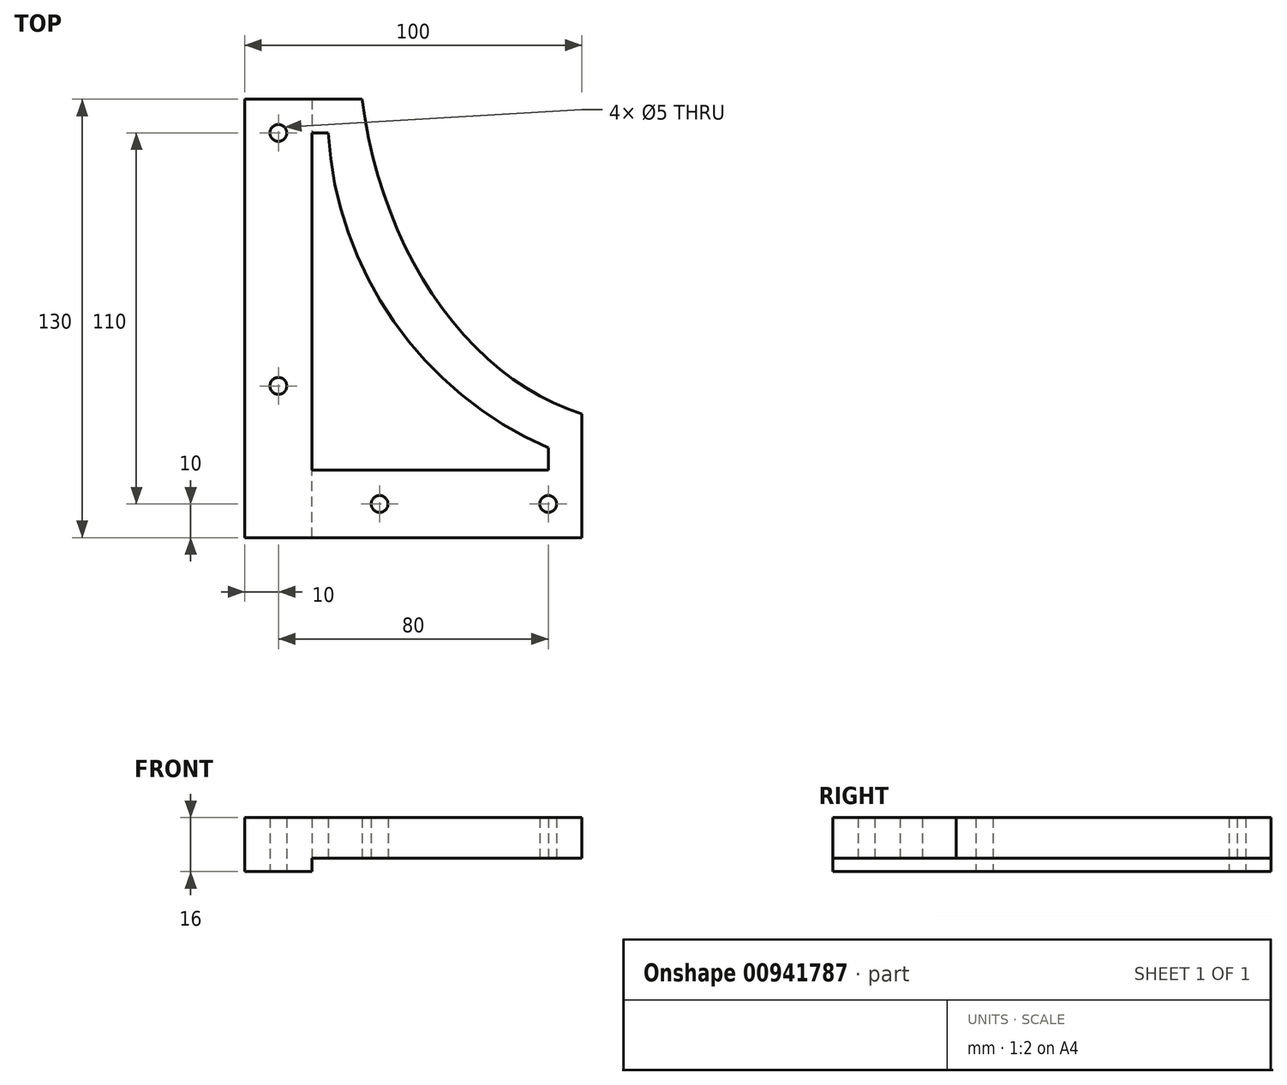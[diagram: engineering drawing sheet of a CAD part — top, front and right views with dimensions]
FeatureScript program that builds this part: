
annotation { "Feature Type Name" : "Feature", "Feature Type Description" : "" }
export const myFeature = defineFeature(function(context is Context, id is Id, definition is map)
    precondition{}
    {
        {
            var Q0;
            Q0=qCreatedBy(makeId("Top.planeOp"),FACE);
            var sketch = newSketch(context, id + "F0", { "sketchPlane" : qUnion([Q0])});
            skEllipticalArc(sketch, "E0", {});
            skLineSegment(sketch, "E1", {"start": v(-86.5, 0) * mm, "end": v(-86.5, -116.5) * mm});
            skPoint(sketch, "E1.endSnap0", {"position": v(0, -116.5) * mm});
            skLineSegment(sketch, "E2", {"start": v(-86.5, -116.5) * mm, "end": v(0, -116.5) * mm});
            skLineSegment(sketch, "E3", {"start": v(-86.5, 0) * mm, "end": v(-100, 0) * mm});
            skLineSegment(sketch, "E4", {"start": v(-100, 0) * mm, "end": v(-100, -130) * mm});
            skLineSegment(sketch, "E5", {"start": v(-100, -130) * mm, "end": v(0, -130) * mm});
            skLineSegment(sketch, "E6", {"start": v(0, -130) * mm, "end": v(0, -116.5) * mm});
            const initialGuessF0  = {"E0": [0, 0, 1, 0, 0.0865, 0.1165, 3.141592653589793, 4.71238898038469]};
            skSetInitialGuess(sketch, initialGuessF0);
            skSolve(sketch);
        }
        {
            var Q0;
            Q0=qSketchRegion(id+"F0",true);
            extrude(context, id + "F1", {"entities" : qUnion([Q0]), "depth" : 12 * mm, "offsetDistance" : 25 * mm});
        }
        {
            var Q0;
            Q0=makeQuery(id+"F1.opExtrude","SWEPT_FACE",FACE,{"disambiguationData":[OSD([sQuery(id+"F0.wireOp",EDGE,"E5")])]});
            var sketch = newSketch(context, id + "F2", { "sketchPlane" : qUnion([Q0])});
            skLineSegment(sketch, "E7.bottom", {"start": v(-100, 16) * mm, "end": v(0, 16) * mm});
            skLineSegment(sketch, "E7.top", {"start": v(-100, -4) * mm, "end": v(0, -4) * mm});
            skLineSegment(sketch, "E7.left", {"start": v(-100, 16) * mm, "end": v(-100, -4) * mm});
            skLineSegment(sketch, "E7.right", {"start": v(0, 16) * mm, "end": v(0, -4) * mm});
            skSolve(sketch);
        }
        {
            var Q0;
            Q0=qSketchRegion(id+"F2",true);
            extrude(context, id + "F3", {"entities" : qUnion([Q0]), "operationType" : NewBodyOperationType.ADD, "depth" : 5 * mm, "offsetDistance" : 25 * mm});
        }
        {
            var Q0;
            Q0=makeQuery(id+"F3.boolean.opBoolean","MERGE",FACE,{"derivedFrom":[makeQuery(id+"F1.opExtrude","SWEPT_FACE",FACE,{"disambiguationData":[OSD([sQuery(id+"F0.wireOp",EDGE,"E4")])]}),makeQuery(id+"F3.opExtrude","SWEPT_FACE",FACE,{"disambiguationData":[OSD([sQuery(id+"F2.wireOp",EDGE,"E7.left")])]})]});
            var sketch = newSketch(context, id + "F4", { "sketchPlane" : qUnion([Q0])});
            skLineSegment(sketch, "E8.bottom", {"start": v(135, 16) * mm, "end": v(0, 16) * mm});
            skLineSegment(sketch, "E8.top", {"start": v(135, -4) * mm, "end": v(0, -4) * mm});
            skLineSegment(sketch, "E8.left", {"start": v(135, 16) * mm, "end": v(135, -4) * mm});
            skLineSegment(sketch, "E8.right", {"start": v(0, 16) * mm, "end": v(0, -4) * mm});
            skSolve(sketch);
        }
        {
            var Q0;
            Q0=qSketchRegion(id+"F4",true);
            extrude(context, id + "F5", {"entities" : qUnion([Q0]), "operationType" : NewBodyOperationType.ADD, "depth" : 5 * mm, "offsetDistance" : 25 * mm});
        }
        {
            var Q0;
            Q0=makeQuery(id+"F5.boolean.opBoolean","MERGE",FACE,{"derivedFrom":[makeQuery(id+"F3.opExtrude","SWEPT_FACE",FACE,{"disambiguationData":[OSD([sQuery(id+"F2.wireOp",EDGE,"E7.bottom")])]}),makeQuery(id+"F5.opExtrude","SWEPT_FACE",FACE,{"disambiguationData":[OSD([sQuery(id+"F4.wireOp",EDGE,"E8.bottom")])]})]});
            var sketch = newSketch(context, id + "F6", { "sketchPlane" : qUnion([Q0])});
            skLineSegment(sketch, "E9", {"start": v(-105, 0) * mm, "end": v(-90, 0) * mm});
            skLineSegment(sketch, "E10", {"start": v(-90, 0) * mm, "end": v(-90, -120) * mm});
            skLineSegment(sketch, "E11", {"start": v(-90, -120) * mm, "end": v(0, -120) * mm});
            skLineSegment(sketch, "E12", {"start": v(0, -120) * mm, "end": v(0, -135) * mm});
            skLineSegment(sketch, "E13", {"start": v(0, -135) * mm, "end": v(-105, -135) * mm});
            skLineSegment(sketch, "E14", {"start": v(-105, -135) * mm, "end": v(-105, 0) * mm});
            skSolve(sketch);
        }
        {
            var Q0;
            Q0=makeQuery(id+"F5.boolean.opBoolean","MERGE",FACE,{"derivedFrom":[makeQuery(id+"F3.opExtrude","SWEPT_FACE",FACE,{"disambiguationData":[OSD([sQuery(id+"F2.wireOp",EDGE,"E7.top")])]}),makeQuery(id+"F5.opExtrude","SWEPT_FACE",FACE,{"disambiguationData":[OSD([sQuery(id+"F4.wireOp",EDGE,"E8.top")])]})]});
            var sketch = newSketch(context, id + "F7", { "sketchPlane" : qUnion([Q0])});
            skLineSegment(sketch, "E15", {"start": v(0, 150) * mm, "end": v(-120, 150) * mm});
            skLineSegment(sketch, "E16", {"start": v(-120, 150) * mm, "end": v(-120, 0) * mm});
            skLineSegment(sketch, "E17", {"start": v(-120, 0) * mm, "end": v(-105, 0) * mm});
            skLineSegment(sketch, "E18", {"start": v(-105, 0) * mm, "end": v(-105, 135) * mm});
            skLineSegment(sketch, "E19", {"start": v(-105, 135) * mm, "end": v(0, 135) * mm});
            skLineSegment(sketch, "E20", {"start": v(0, 135) * mm, "end": v(0, 150) * mm});
            skCircle(sketch, "E21", {"center": v(-110, 30) * mm, "radius": 2.5 * mm});
            skCircle(sketch, "E22", {"center": v(-110, 105) * mm, "radius": 2.5 * mm});
            skCircle(sketch, "E23", {"center": v(-80, 140) * mm, "radius": 2.5 * mm});
            skCircle(sketch, "E24", {"center": v(-30, 140) * mm, "radius": 2.5 * mm});
            skSolve(sketch);
        }
        {
            var Q0;
            Q0=qSketchRegion(id+"F7",true);
            extrude(context, id + "F8", {"entities" : qUnion([Q0]), "operationType" : NewBodyOperationType.ADD, "oppositeDirection" : true, "depth" : 25 * mm, "offsetDistance" : 25 * mm});
        }
        {
            var Q0;
            Q0=qSketchRegion(id+"F6",true);
            extrude(context, id + "F9", {"entities" : qUnion([Q0]), "operationType" : NewBodyOperationType.ADD, "depth" : 5 * mm, "offsetDistance" : 25 * mm});
        }
        {
            var Q0;
            Q0=qCreatedBy(makeId("Top.planeOp"),FACE);
            var sketch = newSketch(context, id + "F10", { "sketchPlane" : qUnion([Q0])});
            skLineSegment(sketch, "E25.bottom", {"start": v(0, 0) * mm, "end": v(-120, 0) * mm});
            skLineSegment(sketch, "E25.top", {"start": v(0, -20) * mm, "end": v(-120, -20) * mm});
            skLineSegment(sketch, "E25.left", {"start": v(0, 0) * mm, "end": v(0, -20) * mm});
            skLineSegment(sketch, "E25.right", {"start": v(-120, 0) * mm, "end": v(-120, -20) * mm});
            skLineSegment(sketch, "E26.bottom", {"start": v(0, 0) * mm, "end": v(-20, 0) * mm});
            skLineSegment(sketch, "E26.top", {"start": v(0, -150) * mm, "end": v(-20, -150) * mm});
            skLineSegment(sketch, "E26.left", {"start": v(0, 0) * mm, "end": v(0, -150) * mm});
            skLineSegment(sketch, "E26.right", {"start": v(-20, 0) * mm, "end": v(-20, -150) * mm});
            skSolve(sketch);
        }
        {
            var Q0;
            Q0=qSketchRegion(id+"F10",true);
            extrude(context, id + "F11", {"entities" : qUnion([Q0]), "operationType" : NewBodyOperationType.REMOVE, "endBound" : BoundingType.SYMMETRIC, "oppositeDirection" : true, "depth" : 50 * mm, "offsetDistance" : 25 * mm});
        }
        {
            var Q0;
            Q0=makeQuery(id+"F11.boolean.opBoolean","COPY",FACE,{"derivedFrom":makeQuery(id+"F11.opExtrude","SWEPT_FACE",FACE,{"disambiguationData":[OSD([sQuery(id+"F10.wireOp",EDGE,"E26.right")])]})});
            var sketch = newSketch(context, id + "F12", { "sketchPlane" : qUnion([Q0])});
            skLineSegment(sketch, "E27.bottom", {"start": v(-150, 21) * mm, "end": v(-20, 21) * mm});
            skLineSegment(sketch, "E27.top", {"start": v(-150, 12) * mm, "end": v(-20, 12) * mm});
            skLineSegment(sketch, "E27.left", {"start": v(-150, 21) * mm, "end": v(-150, 12) * mm});
            skLineSegment(sketch, "E27.right", {"start": v(-20, 21) * mm, "end": v(-20, 12) * mm});
            skSolve(sketch);
        }
        {
            var Q0;
            Q0=qSketchRegion(id+"F12",true);
            extrude(context, id + "F13", {"entities" : qUnion([Q0]), "operationType" : NewBodyOperationType.REMOVE, "endBound" : BoundingType.THROUGH_ALL, "oppositeDirection" : true, "depth" : 25 * mm, "offsetDistance" : 25 * mm});
        }
        {
            var Q0;
            Q0=makeQuery(id+"F1.opExtrude","CAP_FACE",FACE,{"disambiguationData":[OSD([sQuery(id+"F0.wireOp",EDGE,"E0"),sQuery(id+"F0.wireOp",EDGE,"E3"),sQuery(id+"F0.wireOp",EDGE,"E4"),sQuery(id+"F0.wireOp",EDGE,"E5"),sQuery(id+"F0.wireOp",EDGE,"E6")])],"isStart":true});
            var sketch = newSketch(context, id + "F14", { "sketchPlane" : qUnion([Q0])});
            skPoint(sketch, "E28.startSnap0", {"position": v(-20, 121.67) * mm});
            skLineSegment(sketch, "E29", {"start": v(-100, 130) * mm, "end": v(-100, 30) * mm});
            skLineSegment(sketch, "E30", {"start": v(-100, 30) * mm, "end": v(-95.22, 30) * mm});
            skLineSegment(sketch, "E31", {"start": v(-100, 130) * mm, "end": v(-30, 130) * mm});
            skLineSegment(sketch, "E32", {"start": v(-30, 130) * mm, "end": v(-30, 123.34) * mm});
            skArc(sketch, "E33", {"start": v(-30, 123.34) * mm, "mid": v(-75.82, 85.9) * mm, "end": v(-95.22, 30) * mm});
            skSolve(sketch);
        }
        {
            var Q0;
            Q0=qSketchRegion(id+"F14",true);
            extrude(context, id + "F15", {"entities" : qUnion([Q0]), "operationType" : NewBodyOperationType.REMOVE, "endBound" : BoundingType.THROUGH_ALL, "oppositeDirection" : true, "depth" : 25 * mm, "offsetDistance" : 25 * mm});
        }
        {
            var Q0;
            {var subQ1=sQuery(id+"F2.wireOp",EDGE,"E7.top");var subQ3=sQuery(id+"F2.wireOp",EDGE,"E7.right");var subQ4=sQuery(id+"F2.wireOp",EDGE,"E7.left");Q0=makeQuery(id+"F15.boolean.opBoolean","MERGE",FACE,{"derivedFrom":[makeQuery(id+"F3.boolean.opBoolean","SPLIT",FACE,{"disambiguationData":[TD([makeQuery(id+"F3.opExtrude","SWEPT_FACE",FACE,{"disambiguationData":[OSD([subQ1])]})])],"derivedFrom":makeQuery(id+"F3.opExtrude","CAP_FACE",FACE,{"disambiguationData":[OSD([sQuery(id+"F2.wireOp",EDGE,"E7.bottom"),subQ1,subQ4,subQ3])],"isStart":true})})],"fromTools":[makeQuery(id+"F15.opExtrude","SWEPT_FACE",FACE,{"disambiguationData":[OSD([sQuery(id+"F14.wireOp",EDGE,"E31")])]})]});}
            var sketch = newSketch(context, id + "F16", { "sketchPlane" : qUnion([Q0])});
            skLineSegment(sketch, "E34.bottom", {"start": v(20, -4) * mm, "end": v(20, -4) * mm});
            skLineSegment(sketch, "E34.top", {"start": v(20, 0) * mm, "end": v(20, 0) * mm});
            skLineSegment(sketch, "E34.left", {"start": v(20, -4) * mm, "end": v(20, 0) * mm});
            skLineSegment(sketch, "E34.right", {"start": v(20, -4) * mm, "end": v(20, 0) * mm});
            skLineSegment(sketch, "E35.bottom", {"start": v(100, 0) * mm, "end": v(100, 0) * mm});
            skLineSegment(sketch, "E35.top", {"start": v(100, -4) * mm, "end": v(100, -4) * mm});
            skLineSegment(sketch, "E35.left", {"start": v(100, 0) * mm, "end": v(100, -4) * mm});
            skLineSegment(sketch, "E35.right", {"start": v(100, 0) * mm, "end": v(100, -4) * mm});
            skLineSegment(sketch, "E36.bottom", {"start": v(20, -4) * mm, "end": v(100, -4) * mm});
            skLineSegment(sketch, "E36.top", {"start": v(20, 0) * mm, "end": v(100, 0) * mm});
            skLineSegment(sketch, "E36.right", {"start": v(100, -4) * mm, "end": v(100, 0) * mm});
            skSolve(sketch);
        }
        {
            var Q0;
            Q0 = qSketchRegion(id + "F16", true);
            extrude(context, id + "F17", {"entities" : qUnion([Q0]), "operationType" : NewBodyOperationType.REMOVE, "endBound" : BoundingType.UP_TO_NEXT, "oppositeDirection" : true, "depth" : 25 * mm, "offsetDistance" : 25 * mm});
        }
    });
